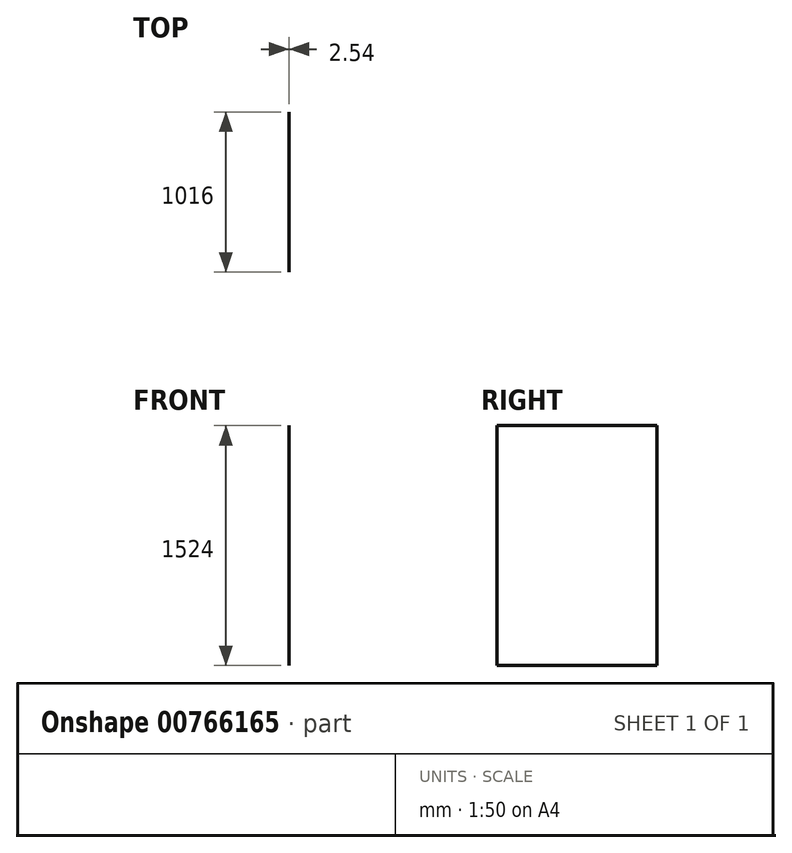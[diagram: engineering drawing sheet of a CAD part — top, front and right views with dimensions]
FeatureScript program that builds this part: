
annotation { "Feature Type Name" : "Feature", "Feature Type Description" : "" }
export const myFeature = defineFeature(function(context is Context, id is Id, definition is map)
    precondition{}
    {
        {
            var Q0;
            Q0=qCreatedBy(makeId("Right.planeOp"),FACE);
            var sketch = newSketch(context, id + "F0", { "sketchPlane" : qUnion([Q0])});
            skLineSegment(sketch, "E0.bottom", {"start": v(508, -762) * mm, "end": v(-508, -762) * mm});
            skLineSegment(sketch, "E0.top", {"start": v(508, 762) * mm, "end": v(-508, 762) * mm});
            skLineSegment(sketch, "E0.left", {"start": v(508, -762) * mm, "end": v(508, 762) * mm});
            skLineSegment(sketch, "E0.right", {"start": v(-508, -762) * mm, "end": v(-508, 762) * mm});
            skPoint(sketch, "E0.middle", {"position": v(0, 0) * mm});
            skSolve(sketch);
        }
        {
            var Q0;
            Q0=makeQuery(id+"F0.imprint","IMPRINT",FACE,{"disambiguationData":[TD([[makeQuery(id+"F0.imprint","IMPRINT",EDGE,{"derivedFrom":sQuery(id+"F0.wireOp",EDGE,"E0.bottom")}),-1.0]])]});
            extrude(context, id + "F1", {"entities" : qUnion([Q0]), "depth" : 2.54 * mm, "offsetDistance" : 25.4 * mm});
        }
    });
